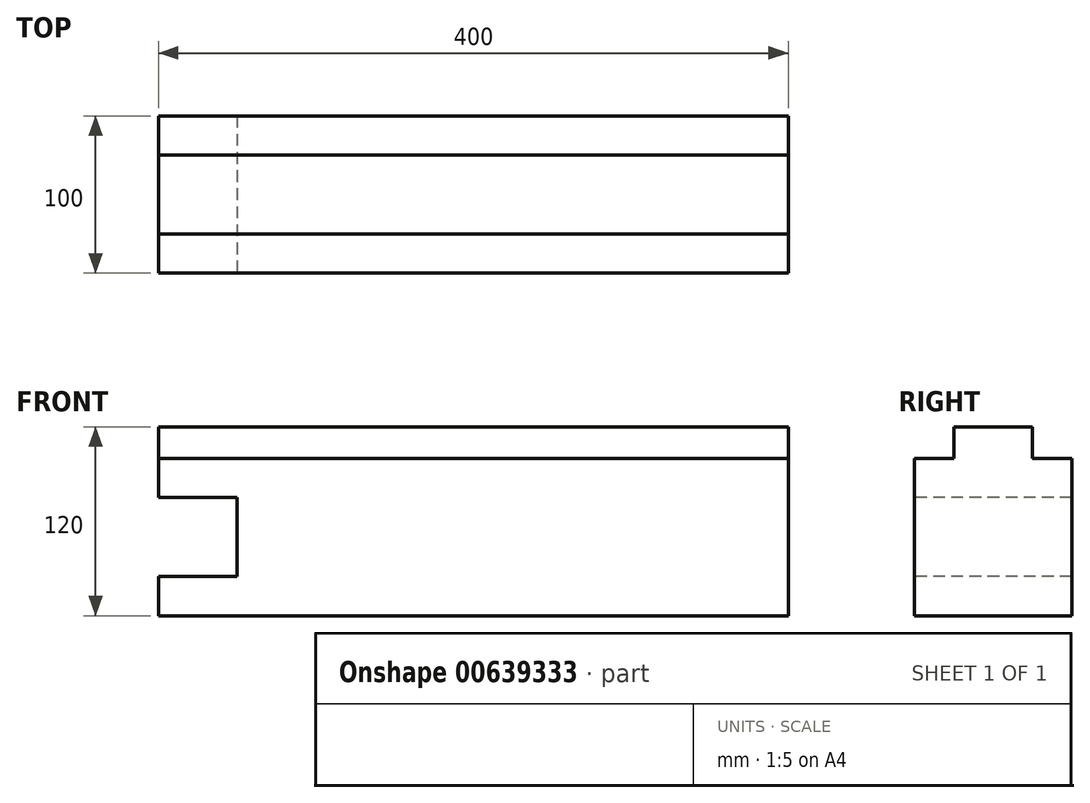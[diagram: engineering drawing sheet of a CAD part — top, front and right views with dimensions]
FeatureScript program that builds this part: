
annotation { "Feature Type Name" : "Feature", "Feature Type Description" : "" }
export const myFeature = defineFeature(function(context is Context, id is Id, definition is map)
    precondition{}
    {
        {
            var Q0;
            Q0=qCreatedBy(makeId("Top.planeOp"),FACE);
            var sketch = newSketch(context, id + "F0", { "sketchPlane" : qUnion([Q0])});
            skLineSegment(sketch, "E0.bottom", {"start": v(-195.63, 4.9) * mm, "end": v(204.37, 4.9) * mm});
            skLineSegment(sketch, "E0.top", {"start": v(-195.63, -95.1) * mm, "end": v(204.37, -95.1) * mm});
            skLineSegment(sketch, "E0.left", {"start": v(-195.63, 4.9) * mm, "end": v(-195.63, -95.1) * mm});
            skLineSegment(sketch, "E0.right", {"start": v(204.37, 4.9) * mm, "end": v(204.37, -95.1) * mm});
            skSolve(sketch);
        }
        {
            var Q0;
            Q0 = qSketchRegion(id + "F0", true);
            extrude(context, id + "F1", {"entities" : qUnion([Q0]), "depth" : 120 * mm, "offsetDistance" : 25 * mm});
        }
        {
            var Q0;
            Q0=makeQuery(id+"F1.opExtrude","CAP_FACE",FACE,{"disambiguationData":[OSD([sQuery(id+"F0.wireOp",EDGE,"E0.bottom"),sQuery(id+"F0.wireOp",EDGE,"E0.top"),sQuery(id+"F0.wireOp",EDGE,"E0.left"),sQuery(id+"F0.wireOp",EDGE,"E0.right")])],"isStart":false});
            var sketch = newSketch(context, id + "F2", { "sketchPlane" : qUnion([Q0])});
            skLineSegment(sketch, "E1.bottom", {"start": v(-195.63, 4.9) * mm, "end": v(204.37, 4.9) * mm});
            skLineSegment(sketch, "E1.top", {"start": v(-195.63, -20.1) * mm, "end": v(204.37, -20.1) * mm});
            skLineSegment(sketch, "E1.left", {"start": v(-195.63, 4.9) * mm, "end": v(-195.63, -20.1) * mm});
            skLineSegment(sketch, "E1.right", {"start": v(204.37, 4.9) * mm, "end": v(204.37, -20.1) * mm});
            skLineSegment(sketch, "E2.bottom", {"start": v(-195.63, -95.1) * mm, "end": v(204.37, -95.1) * mm});
            skLineSegment(sketch, "E2.top", {"start": v(-195.63, -70.1) * mm, "end": v(204.37, -70.1) * mm});
            skLineSegment(sketch, "E2.left", {"start": v(-195.63, -95.1) * mm, "end": v(-195.63, -70.1) * mm});
            skLineSegment(sketch, "E2.right", {"start": v(204.37, -95.1) * mm, "end": v(204.37, -70.1) * mm});
            skSolve(sketch);
        }
        {
            var Q0;
            Q0 = qSketchRegion(id + "F2", true);
            extrude(context, id + "F3", {"entities" : qUnion([Q0]), "operationType" : NewBodyOperationType.REMOVE, "oppositeDirection" : true, "depth" : 20 * mm, "offsetDistance" : 25 * mm});
        }
        {
            var Q0;
            Q0=makeQuery(id+"F1.opExtrude","SWEPT_FACE",FACE,{"disambiguationData":[OSD([sQuery(id+"F0.wireOp",EDGE,"E0.left")])]});
            var sketch = newSketch(context, id + "F4", { "sketchPlane" : qUnion([Q0])});
            skLineSegment(sketch, "E3.bottom", {"start": v(-4.9, 75) * mm, "end": v(95.1, 75) * mm});
            skLineSegment(sketch, "E3.top", {"start": v(-4.9, 25) * mm, "end": v(95.1, 25) * mm});
            skLineSegment(sketch, "E3.left", {"start": v(-4.9, 75) * mm, "end": v(-4.9, 25) * mm});
            skLineSegment(sketch, "E3.right", {"start": v(95.1, 75) * mm, "end": v(95.1, 25) * mm});
            skSolve(sketch);
        }
        {
            var Q0;
            Q0 = qSketchRegion(id + "F4", true);
            extrude(context, id + "F5", {"entities" : qUnion([Q0]), "operationType" : NewBodyOperationType.REMOVE, "oppositeDirection" : true, "depth" : 50 * mm, "offsetDistance" : 25 * mm});
        }
    });
